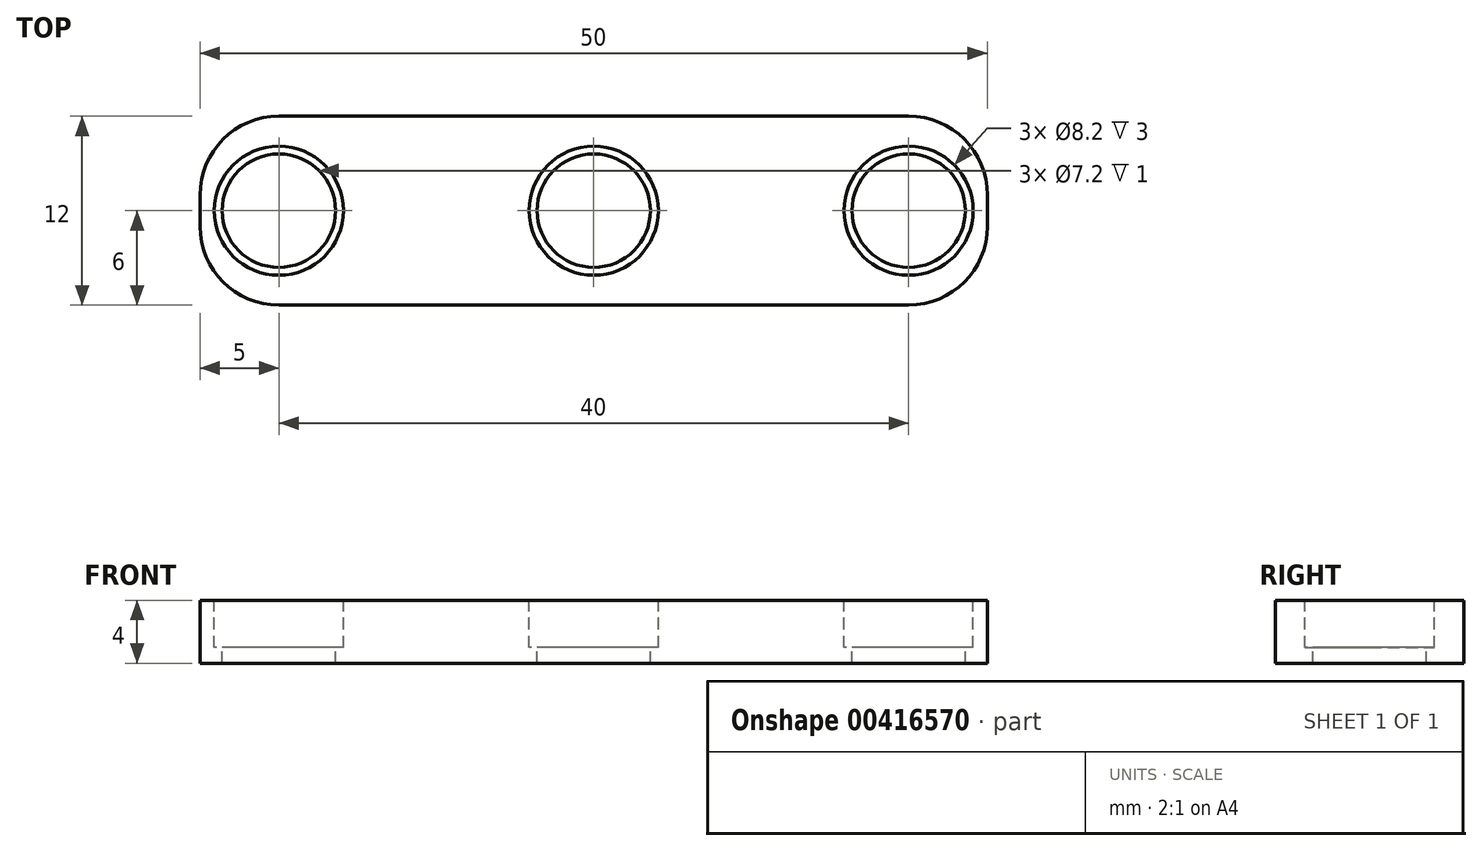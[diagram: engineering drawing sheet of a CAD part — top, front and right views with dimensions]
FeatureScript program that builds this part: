
annotation { "Feature Type Name" : "Feature", "Feature Type Description" : "" }
export const myFeature = defineFeature(function(context is Context, id is Id, definition is map)
    precondition{}
    {
        {
            var Q0;
            Q0=qCreatedBy(makeId("Top.planeOp"),FACE);
            var sketch = newSketch(context, id + "F0", { "sketchPlane" : qUnion([Q0])});
            skLineSegment(sketch, "E0.bottom", {"start": v(-19.88, 0) * mm, "end": v(30.12, 0) * mm});
            skLineSegment(sketch, "E0.top", {"start": v(-19.88, 12) * mm, "end": v(30.12, 12) * mm});
            skLineSegment(sketch, "E0.left", {"start": v(-19.88, 0) * mm, "end": v(-19.88, 12) * mm});
            skLineSegment(sketch, "E0.right", {"start": v(30.12, 0) * mm, "end": v(30.12, 12) * mm});
            skSolve(sketch);
        }
        {
            var Q0;
            Q0=makeQuery(id+"F0.imprint","IMPRINT",FACE,{"disambiguationData":[TD([[makeQuery(id+"F0.imprint","IMPRINT",EDGE,{"derivedFrom":sQuery(id+"F0.wireOp",EDGE,"E0.bottom")}),1.0]])]});
            extrude(context, id + "F1", {"entities" : qUnion([Q0]), "depth" : 4 * mm});
        }
        {
            var Q0;
            Q0=makeQuery(id+"F1.opExtrude","CAP_FACE",FACE,{"disambiguationData":[OSD([sQuery(id+"F0.wireOp",EDGE,"E0.bottom"),sQuery(id+"F0.wireOp",EDGE,"E0.top"),sQuery(id+"F0.wireOp",EDGE,"E0.left"),sQuery(id+"F0.wireOp",EDGE,"E0.right")])],"isStart":false});
            var sketch = newSketch(context, id + "F2", { "sketchPlane" : qUnion([Q0])});
            skCircle(sketch, "E1", {"center": v(25.12, 6) * mm, "radius": 4.1 * mm});
            skCircle(sketch, "E2", {"center": v(-14.88, 6) * mm, "radius": 4.1 * mm});
            skCircle(sketch, "E3", {"center": v(5.12, 6) * mm, "radius": 4.1 * mm});
            skCircle(sketch, "E4", {"center": v(5.12, 6) * mm, "radius": 3.6 * mm});
            skCircle(sketch, "E5", {"center": v(25.12, 6) * mm, "radius": 3.6 * mm});
            skCircle(sketch, "E6", {"center": v(-14.88, 6) * mm, "radius": 3.6 * mm});
            skSolve(sketch);
        }
        {
            var Q0;
            Q0=makeQuery(id+"F2.imprint","IMPRINT",FACE,{"disambiguationData":[TD([[makeQuery(id+"F2.imprint","IMPRINT",EDGE,{"derivedFrom":sQuery(id+"F2.wireOp",EDGE,"E2")}),1.0]])]});
            var Q1;
            Q1=makeQuery(id+"F2.imprint","IMPRINT",FACE,{"disambiguationData":[TD([[makeQuery(id+"F2.imprint","IMPRINT",EDGE,{"derivedFrom":sQuery(id+"F2.wireOp",EDGE,"E3")}),1.0]])]});
            var Q2;
            Q2=makeQuery(id+"F2.imprint","IMPRINT",FACE,{"disambiguationData":[TD([[makeQuery(id+"F2.imprint","IMPRINT",EDGE,{"derivedFrom":sQuery(id+"F2.wireOp",EDGE,"E1")}),1.0]])]});
            extrude(context, id + "F3", {"entities" : qUnion([Q0, Q1, Q2]), "operationType" : NewBodyOperationType.REMOVE, "oppositeDirection" : true, "depth" : 3 * mm});
        }
        {
            var Q0;
            Q0=makeQuery(id+"F2.imprint","IMPRINT",FACE,{"disambiguationData":[TD([[makeQuery(id+"F2.imprint","IMPRINT",EDGE,{"derivedFrom":sQuery(id+"F2.wireOp",EDGE,"E6")}),1.0]])]});
            var Q1;
            Q1=makeQuery(id+"F2.imprint","IMPRINT",FACE,{"disambiguationData":[TD([[makeQuery(id+"F2.imprint","IMPRINT",EDGE,{"derivedFrom":sQuery(id+"F2.wireOp",EDGE,"E4")}),1.0]])]});
            var Q2;
            Q2=makeQuery(id+"F2.imprint","IMPRINT",FACE,{"disambiguationData":[TD([[makeQuery(id+"F2.imprint","IMPRINT",EDGE,{"derivedFrom":sQuery(id+"F2.wireOp",EDGE,"E5")}),1.0]])]});
            extrude(context, id + "F4", {"entities" : qUnion([Q0, Q1, Q2]), "operationType" : NewBodyOperationType.REMOVE, "oppositeDirection" : true, "depth" : 25 * mm});
        }
        {
            var Q0;
            Q0=makeQuery(id+"F1.opExtrude","SWEPT_EDGE",EDGE,{"disambiguationData":[OSD([sQuery(id+"F0.wireOp",EDGE,"E0.top"),sQuery(id+"F0.wireOp",EDGE,"E0.right")])]});
            var Q1;
            Q1=makeQuery(id+"F1.opExtrude","SWEPT_EDGE",EDGE,{"disambiguationData":[OSD([sQuery(id+"F0.wireOp",EDGE,"E0.bottom"),sQuery(id+"F0.wireOp",EDGE,"E0.right")])]});
            var Q2;
            Q2=makeQuery(id+"F1.opExtrude","SWEPT_EDGE",EDGE,{"disambiguationData":[OSD([sQuery(id+"F0.wireOp",EDGE,"E0.top"),sQuery(id+"F0.wireOp",EDGE,"E0.left")])]});
            var Q3;
            Q3=makeQuery(id+"F1.opExtrude","SWEPT_EDGE",EDGE,{"disambiguationData":[OSD([sQuery(id+"F0.wireOp",EDGE,"E0.bottom"),sQuery(id+"F0.wireOp",EDGE,"E0.left")])]});
            fillet(context, id + "F5", {"entities" : qUnion([Q0, Q1, Q2, Q3]), "radius" : 5 * mm, "tangentPropagation" : true, "allowEdgeOverflow" : false});
        }
    });
